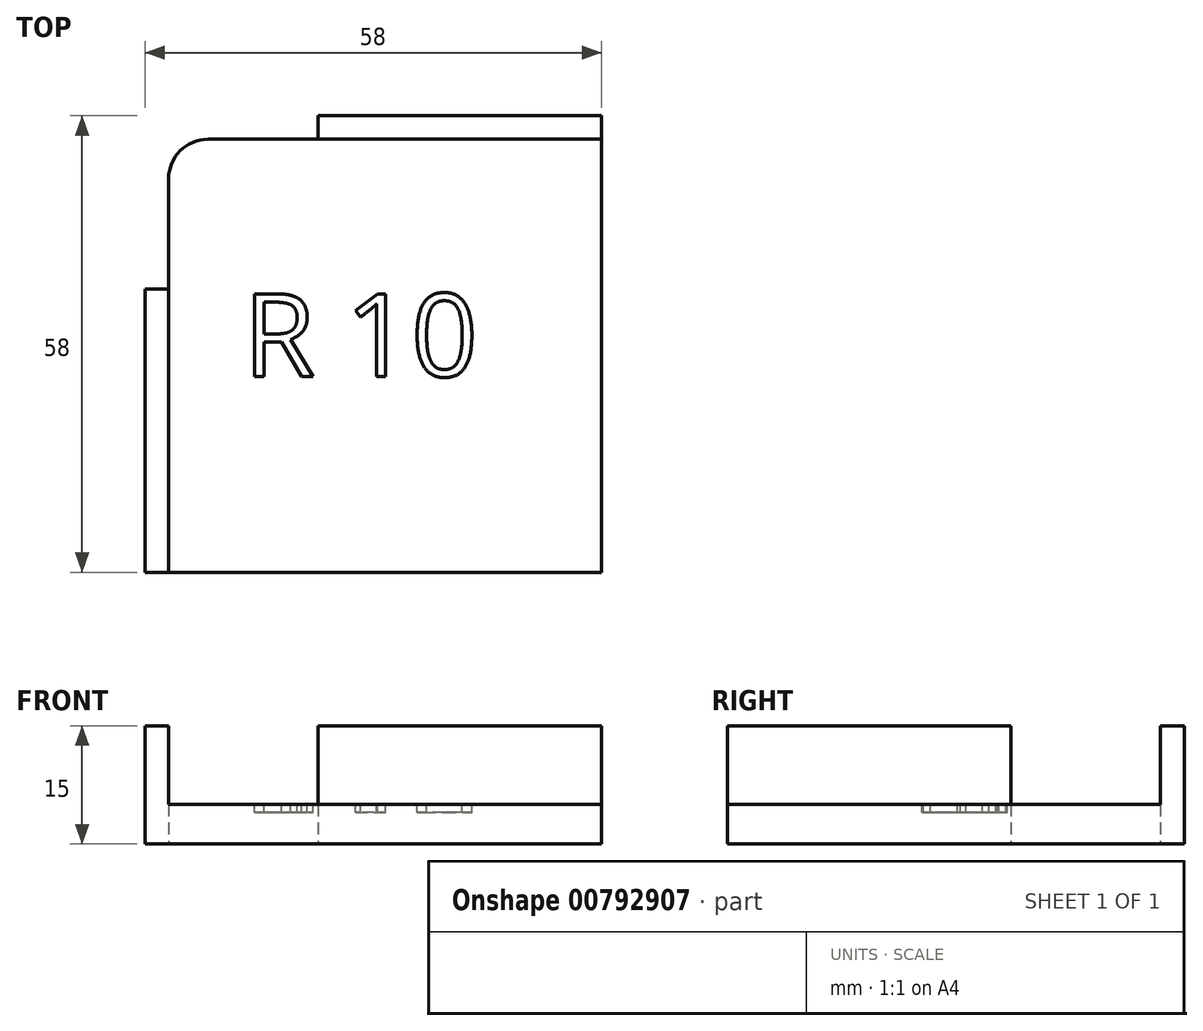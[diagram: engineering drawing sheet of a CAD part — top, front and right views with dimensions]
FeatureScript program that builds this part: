
annotation { "Feature Type Name" : "Feature", "Feature Type Description" : "" }
export const myFeature = defineFeature(function(context is Context, id is Id, definition is map)
    precondition{}
    {
        {
            var Q0;
            Q0=qCreatedBy(makeId("Top.planeOp"),FACE);
            var sketch = newSketch(context, id + "F0", { "sketchPlane" : qUnion([Q0])});
            skArc(sketch, "E0", {"start": v(0, 5) * mm, "mid": v(-3.54, 3.54) * mm, "end": v(-5, 0) * mm});
            skLineSegment(sketch, "E1", {"start": v(0, 5) * mm, "end": v(50, 5) * mm});
            skLineSegment(sketch, "E2", {"start": v(50, 5) * mm, "end": v(50, -50) * mm});
            skLineSegment(sketch, "E3", {"start": v(50, -50) * mm, "end": v(-5, -50) * mm});
            skLineSegment(sketch, "E4", {"start": v(-5, -50) * mm, "end": v(-5, 0) * mm});
            skSolve(sketch);
        }
        {
            var Q0;
            Q0=qSketchRegion(id+"F0",true);
            extrude(context, id + "F1", {"entities" : qUnion([Q0]), "depth" : 5 * mm, "offsetDistance" : 25 * mm});
        }
        {
            var Q0;
            Q0=makeQuery(id+"F1.opExtrude","CAP_FACE",FACE,{"disambiguationData":[OSD([sQuery(id+"F0.wireOp",EDGE,"E0"),sQuery(id+"F0.wireOp",EDGE,"E1"),sQuery(id+"F0.wireOp",EDGE,"E2"),sQuery(id+"F0.wireOp",EDGE,"E3"),sQuery(id+"F0.wireOp",EDGE,"E4")])],"isStart":false});
            var sketch = newSketch(context, id + "F2", { "sketchPlane" : qUnion([Q0])});
            skLineSegment(sketch, "E5.bottom", {"start": v(-5, -50) * mm, "end": v(-8, -50) * mm});
            skLineSegment(sketch, "E5.top", {"start": v(-5, -14) * mm, "end": v(-8, -14) * mm});
            skLineSegment(sketch, "E5.left", {"start": v(-5, -50) * mm, "end": v(-5, -14) * mm});
            skLineSegment(sketch, "E5.right", {"start": v(-8, -50) * mm, "end": v(-8, -14) * mm});
            skLineSegment(sketch, "E6.bottom", {"start": v(50, 5) * mm, "end": v(14, 5) * mm});
            skLineSegment(sketch, "E6.top", {"start": v(50, 8) * mm, "end": v(14, 8) * mm});
            skLineSegment(sketch, "E6.left", {"start": v(50, 5) * mm, "end": v(50, 8) * mm});
            skLineSegment(sketch, "E6.right", {"start": v(14, 5) * mm, "end": v(14, 8) * mm});
            skSolve(sketch);
        }
        {
            var Q0;
            Q0=qSketchRegion(id+"F2",true);
            var Q1;
            Q1=makeQuery(id+"F1.opExtrude","CAP_FACE",FACE,{"disambiguationData":[OSD([sQuery(id+"F0.wireOp",EDGE,"E0"),sQuery(id+"F0.wireOp",EDGE,"E1"),sQuery(id+"F0.wireOp",EDGE,"E2"),sQuery(id+"F0.wireOp",EDGE,"E3"),sQuery(id+"F0.wireOp",EDGE,"E4")])],"isStart":true});
            extrude(context, id + "F3", {"entities" : qUnion([Q0]), "operationType" : NewBodyOperationType.ADD, "depth" : 10 * mm, "offsetDistance" : 25 * mm, "hasSecondDirection" : true, "secondDirectionBound" : SecondDirectionBoundingType.UP_TO_SURFACE, "secondDirectionOppositeDirection" : true, "secondDirectionDepth" : 25 * mm, "secondDirectionBoundEntityFace" : qUnion([Q1])});
        }
        {
            var Q0;
            Q0=makeQuery(id+"F1.opExtrude","CAP_FACE",FACE,{"disambiguationData":[OSD([sQuery(id+"F0.wireOp",EDGE,"E0"),sQuery(id+"F0.wireOp",EDGE,"E1"),sQuery(id+"F0.wireOp",EDGE,"E2"),sQuery(id+"F0.wireOp",EDGE,"E3"),sQuery(id+"F0.wireOp",EDGE,"E4")])],"isStart":false});
            var sketch = newSketch(context, id + "F4", { "sketchPlane" : qUnion([Q0])});
            skText(sketch, "E7", { "text": "R 10", "fontName": "OpenSans-Regular.ttf"});
            const initialGuessF4  = {"E7": [0.00449, -0.02514, 1, 0, 0.0106]};
            skSetInitialGuess(sketch, initialGuessF4);
            skSolve(sketch);
        }
        {
            var Q0;
            Q0=qSketchRegion(id+"F4",true);
            extrude(context, id + "F5", {"entities" : qUnion([Q0]), "operationType" : NewBodyOperationType.REMOVE, "oppositeDirection" : true, "depth" : 1 * mm, "offsetDistance" : 25 * mm});
        }
        {
            var Q0;
            Q0=makeQuery(id+"F1.opExtrude","SWEPT_BODY",BODY,{"disambiguationData":[OSD([sQuery(id+"F0.wireOp",EDGE,"E0"),sQuery(id+"F0.wireOp",EDGE,"E1"),sQuery(id+"F0.wireOp",EDGE,"E2"),sQuery(id+"F0.wireOp",EDGE,"E3"),sQuery(id+"F0.wireOp",EDGE,"E4")])]});
            transform(context, id + "F6", {"entities" : qUnion([Q0]), "transformType" : TransformType.TRANSLATION_3D, "dx" : 0 * mm, "dy" : 0 * mm, "dz" : 0 * mm, "makeCopy" : true});
        }
        {
            var Q0;
            Q0=makeQuery(id+"F6.opPattern","COPY",BODY,{"derivedFrom":makeQuery(id+"F1.opExtrude","SWEPT_BODY",BODY,{"disambiguationData":[OSD([sQuery(id+"F0.wireOp",EDGE,"E0"),sQuery(id+"F0.wireOp",EDGE,"E1"),sQuery(id+"F0.wireOp",EDGE,"E2"),sQuery(id+"F0.wireOp",EDGE,"E3"),sQuery(id+"F0.wireOp",EDGE,"E4")])]}),"instanceName":"1"});
            deleteBodies(context, id + "F7", {"entities" : qUnion([Q0])});
        }
    });
